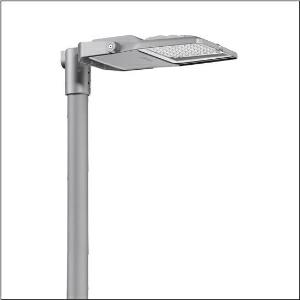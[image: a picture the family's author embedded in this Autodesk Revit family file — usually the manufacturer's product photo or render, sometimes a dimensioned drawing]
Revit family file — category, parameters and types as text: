
# Revit family: floodlight_fl_21_iq_mini___pl52_5xa7772d4d3a_25ab
name_source: partatom
category: Lighting Fixtures
units: mm (PartAtom-declared; Revit-internal decimal feet)

## family parameters
Cut with Voids When Loaded = No
Host = Face
Light Source = No
Part Type = Normal
Room Calculation Point = No
Round Connector Dimension = Use Diameter
Shared = No

## types (1)
- --- (1 x LED, 18610 lm, 143 W, 4000K)
    Apparent Load = 143 VA
    CIE Flux Codes = 26 60 98 100 100
    Color Rendering = 70
    Color Temperature = 4000K
    Default Elevation = 1800 mm
    Description = Floodlight FL 21 iQ mini, floodlight, primary light control with lens, of PMMA, primary optical cover: protective disc, of toughened safety glass, transparent, light distribution: PL52, light emission: direct distribution, installation type: surface-mounted, LED, High Power LED, rated luminous flux: 18.610lm, luminous efficacy: 130lm/W, light colour: 740, colour temperature: 4000K, control: Auto-Match, Temp-Guard, Night-Set, Smart-Wire, Desk-Remote (wireless, voltage-free reading and setting of iQ features in the workshop via application-optimized NFC function/RFID function), optimised constant luminous flux control (CLO 2.0), Light-Fading, Lumen-Switch, with terminal, 6-pole, mains connection: 220..240V, AC, 50/60Hz, start of lifetime: 143W, end of service life: 152W, reduction: 61W, luminaire housing, of diecast aluminium, powder-coated, Siteco® metallic grey (DB 702S), corrosivity category C5 mid according to DIN EN ISO 12944, sealing non-destructively replaceable, please order mast flange separately, mast bracket, of steel, galvanised, powder-coated, protection rating (complete): IP66, insulation class (complete): insulation class II (safety insulation), certification: CE, ENEC, VDE, protection symbol: D, impact resistance: IK08, permissible operating ambient temperature: -40..+40°C, permissible operating ambient temperature for outdoor applications: -40..+50°C, standard: DIN EN 12944, LABS conformity tested according to VDMA 24364:2018-05, packaging unit: 1 piece

Light Distribution: PL52
    Height = 70 mm
    Lamp = 1 x LED
    Lamp Light Flux = 18610 lm
    Lamp Power = 143 W
    Lamp count = 1
    Length = 485 mm
    Luminous efficacy = 130 lm/W
    Manufacturer = Siteco
    ModVariant = No
    Model = 5XA7772D4D3A
    Number of Poles = 1
    OnlyDefault = Yes
    Power Factor = 1
    Product Name = Floodlight FL 21 iQ mini | PL52
    Product group = floodlight | pylon annexe
    ProductGroupID = 6200
    Protection Class = Protection class II
    Protection Degree = IP 66
    RLX_Detail_Level = 1
    RLX_Emergency_Light_Flux = 0 lm
    RLX_Emergency_Type = 0
    RLX_Emergency_Type_DB = No
    RlxData = <blob elided: 101693 chars, md5=c5866ffc>
    Socket = socket
    Standby Power = 0 W
    System Light Flux = 18610 lm
    System Power = 143 W
    Type Comments = factory setting: luminous flux: 100 % | dim-lin: 254 | 730 mA
    Type Image = l_1007125.jpg
    URL = http://relux.com
    VarID = @adj_095859
    Voltage = 0 V
    Weight = 0.00 kg
    Width = 337 mm

## geometry (parser evidence)
native form markers: Blend x4, Sweep x12
no freeform markers — native parametric forms only
